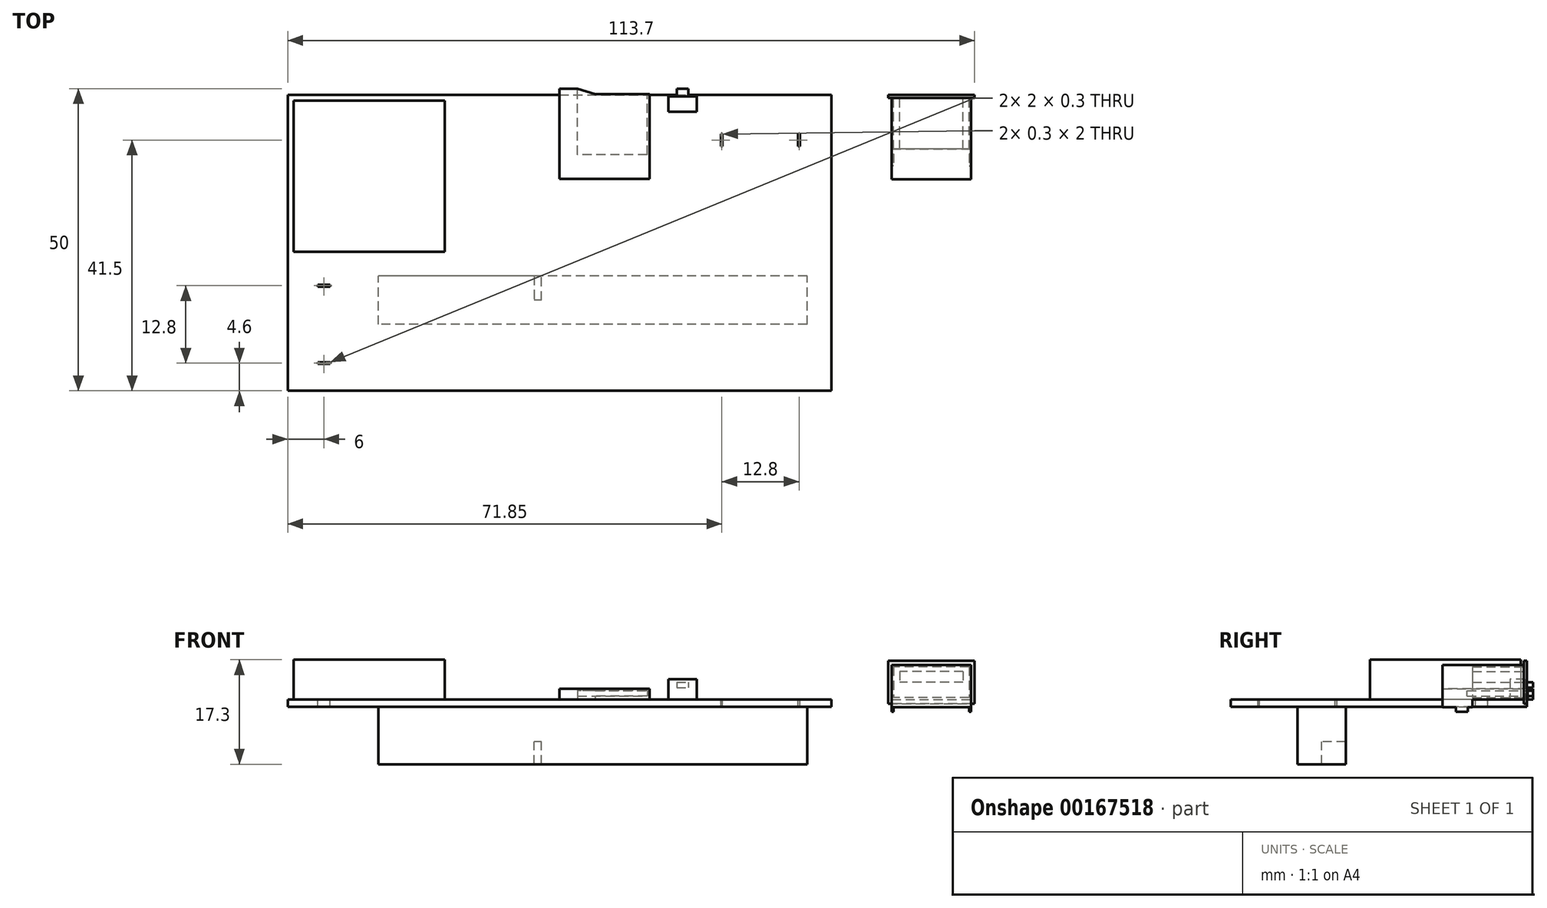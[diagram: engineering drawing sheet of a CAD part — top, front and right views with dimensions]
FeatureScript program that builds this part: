
annotation { "Feature Type Name" : "Feature", "Feature Type Description" : "" }
export const myFeature = defineFeature(function(context is Context, id is Id, definition is map)
    precondition{}
    {
        {
            var Q0;
            Q0=qCreatedBy(makeId("Top.planeOp"),FACE);
            var sketch = newSketch(context, id + "F0", { "sketchPlane" : qUnion([Q0])});
            skLineSegment(sketch, "E0.bottom", {"start": v(0, 0) * mm, "end": v(90, 0) * mm});
            skLineSegment(sketch, "E0.left", {"start": v(0, 0) * mm, "end": v(0, -49) * mm});
            skLineSegment(sketch, "E0.right", {"start": v(90, 0) * mm, "end": v(90, -49) * mm});
            skLineSegment(sketch, "E1.bottom", {"start": v(0, -49) * mm, "end": v(90, -49) * mm});
            skLineSegment(sketch, "E2.bottom", {"start": v(1, -1) * mm, "end": v(26, -1) * mm});
            skLineSegment(sketch, "E2.top", {"start": v(1, -26) * mm, "end": v(26, -26) * mm});
            skLineSegment(sketch, "E2.left", {"start": v(1, -1) * mm, "end": v(1, -26) * mm});
            skLineSegment(sketch, "E2.right", {"start": v(26, -1) * mm, "end": v(26, -26) * mm});
            skLineSegment(sketch, "E3", {"start": v(59.9, 0.1) * mm, "end": v(50.9, 0.1) * mm});
            skLineSegment(sketch, "E4", {"start": v(59.9, 0.1) * mm, "end": v(59.9, -13.9) * mm});
            skLineSegment(sketch, "E5", {"start": v(59.9, -13.9) * mm, "end": v(45, -13.9) * mm});
            skLineSegment(sketch, "E6", {"start": v(45, -13.9) * mm, "end": v(45, 1) * mm});
            skLineSegment(sketch, "E7", {"start": v(45, 1) * mm, "end": v(48, 1) * mm});
            skLineSegment(sketch, "E8", {"start": v(48, 1) * mm, "end": v(50.9, 0.1) * mm});
            skLineSegment(sketch, "E9.bottom", {"start": v(86, -38) * mm, "end": v(15, -38) * mm});
            skLineSegment(sketch, "E9.top", {"start": v(86, -30) * mm, "end": v(15, -30) * mm});
            skLineSegment(sketch, "E9.left", {"start": v(86, -38) * mm, "end": v(86, -30) * mm});
            skLineSegment(sketch, "E9.right", {"start": v(15, -38) * mm, "end": v(15, -30) * mm});
            skLineSegment(sketch, "E10", {"start": v(40.8, -30) * mm, "end": v(40.8, -34) * mm});
            skLineSegment(sketch, "E11", {"start": v(42, -34) * mm, "end": v(40.8, -34) * mm});
            skLineSegment(sketch, "E12", {"start": v(42, -34) * mm, "end": v(42, -30) * mm});
            skLineSegment(sketch, "E13.0.MirrorCS", {"start": v(63, -2.8) * mm, "end": v(67.7, -2.8) * mm});
            skLineSegment(sketch, "E13.1.MirrorCS", {"start": v(66.3, 1) * mm, "end": v(64.4, 1) * mm});
            skLineSegment(sketch, "E13.2.MirrorCS", {"start": v(66.3, -0.3) * mm, "end": v(66.3, 1) * mm});
            skLineSegment(sketch, "E13.3.MirrorCS", {"start": v(64.4, 1) * mm, "end": v(64.4, -0.3) * mm});
            skLineSegment(sketch, "E13.4.MirrorCS", {"start": v(66.3, -0.3) * mm, "end": v(67.7, -0.3) * mm});
            skLineSegment(sketch, "E13.5.MirrorCS", {"start": v(64.4, -0.3) * mm, "end": v(66.3, -0.3) * mm});
            skLineSegment(sketch, "E13.6.MirrorCS", {"start": v(63, -0.3) * mm, "end": v(64.4, -0.3) * mm});
            skLineSegment(sketch, "E13.7.MirrorCS", {"start": v(63, -0.3) * mm, "end": v(63, -2.8) * mm});
            skLineSegment(sketch, "E13.8.MirrorCS", {"start": v(67.7, -0.3) * mm, "end": v(67.7, -2.8) * mm});
            skLineSegment(sketch, "E14", {"start": v(78.25, 0) * mm, "end": v(78.25, -14.14) * mm, "construction": true});
            skLineSegment(sketch, "E15.bottom", {"start": v(71.7, -6.5) * mm, "end": v(72, -6.5) * mm});
            skLineSegment(sketch, "E15.top", {"start": v(71.7, -8.5) * mm, "end": v(72, -8.5) * mm});
            skLineSegment(sketch, "E15.left", {"start": v(71.7, -6.5) * mm, "end": v(71.7, -8.5) * mm});
            skLineSegment(sketch, "E15.right", {"start": v(72, -6.5) * mm, "end": v(72, -8.5) * mm});
            skLineSegment(sketch, "E16.0.MirrorCS", {"start": v(84.8, -6.5) * mm, "end": v(84.5, -6.5) * mm});
            skLineSegment(sketch, "E16.1.MirrorCS", {"start": v(84.8, -6.5) * mm, "end": v(84.8, -8.5) * mm});
            skLineSegment(sketch, "E16.2.MirrorCS", {"start": v(84.5, -6.5) * mm, "end": v(84.5, -8.5) * mm});
            skLineSegment(sketch, "E16.3.MirrorCS", {"start": v(84.8, -8.5) * mm, "end": v(84.5, -8.5) * mm});
            skLineSegment(sketch, "E17", {"start": v(90, -38) * mm, "end": v(0, -38) * mm, "construction": true});
            skLineSegment(sketch, "E18.bottom", {"start": v(7, -31.45) * mm, "end": v(5, -31.45) * mm});
            skLineSegment(sketch, "E18.top", {"start": v(7, -31.75) * mm, "end": v(5, -31.75) * mm});
            skLineSegment(sketch, "E18.left", {"start": v(7, -31.45) * mm, "end": v(7, -31.75) * mm});
            skLineSegment(sketch, "E18.right", {"start": v(5, -31.45) * mm, "end": v(5, -31.75) * mm});
            skLineSegment(sketch, "E19.0.MirrorCS", {"start": v(7, -44.55) * mm, "end": v(7, -44.25) * mm});
            skLineSegment(sketch, "E19.1.MirrorCS", {"start": v(7, -44.25) * mm, "end": v(5, -44.25) * mm});
            skLineSegment(sketch, "E19.2.MirrorCS", {"start": v(7, -44.55) * mm, "end": v(5, -44.55) * mm});
            skLineSegment(sketch, "E19.3.MirrorCS", {"start": v(5, -44.55) * mm, "end": v(5, -44.25) * mm});
            skSolve(sketch);
        }
        {
            var Q0;
            Q0=makeQuery(id+"F0.imprint","IMPRINT",FACE,{"disambiguationData":[TD([[makeQuery(id+"F0.imprint","IMPRINT",EDGE,{"derivedFrom":sQuery(id+"F0.wireOp",EDGE,"E0.bottom")}),-1.0]])]});
            var Q1;
            {var subQ7=sQuery(id+"F0.wireOp",EDGE,"E1.bottom");Q1=makeQuery(id+"F0.imprint","IMPRINT",FACE,{"disambiguationData":[TD([[makeQuery(id+"F0.imprint","IMPRINT",EDGE,{"derivedFrom":subQ7}),-1.0]])]});}
            var Q2;
            Q2=makeQuery(id+"F0.imprint","IMPRINT",FACE,{"disambiguationData":[TD([[makeQuery(id+"F0.imprint","IMPRINT",EDGE,{"derivedFrom":sQuery(id+"F0.wireOp",EDGE,"E2.bottom")}),-1.0]])]});
            var Q3;
            {var subQ3=sQuery(id+"F0.wireOp",EDGE,"E5");Q3=makeQuery(id+"F0.imprint","IMPRINT",FACE,{"disambiguationData":[TD([[makeQuery(id+"F0.imprint","IMPRINT",EDGE,{"derivedFrom":subQ3}),-1.0]])]});}
            var Q4;
            Q4=makeQuery(id+"F0.imprint","IMPRINT",FACE,{"disambiguationData":[TD([[makeQuery(id+"F0.imprint","IMPRINT",EDGE,{"derivedFrom":sQuery(id+"F0.wireOp",EDGE,"E9.bottom")}),-1.0]])]});
            var Q5;
            {var subQ1=sQuery(id+"F0.wireOp",EDGE,"E10");Q5=makeQuery(id+"F0.imprint","IMPRINT",FACE,{"disambiguationData":[TD([[makeQuery(id+"F0.imprint","IMPRINT",EDGE,{"derivedFrom":subQ1}),1.0]])]});}
            var Q6;
            Q6=makeQuery(id+"F0.imprint","IMPRINT",FACE,{"disambiguationData":[TD([[makeQuery(id+"F0.imprint","IMPRINT",EDGE,{"derivedFrom":sQuery(id+"F0.wireOp",EDGE,"E13.0.MirrorCS")}),1.0]])]});
            var Q7;
            {var subQ0=sQuery(id+"F0.wireOp",EDGE,"E13.5.MirrorCS");Q7=makeQuery(id+"F0.imprint","IMPRINT",FACE,{"disambiguationData":[TD([[makeQuery(id+"F0.imprint","IMPRINT",EDGE,{"derivedFrom":subQ0}),1.0]])]});}
            extrude(context, id + "F1", {"entities" : qUnion([Q0, Q1, Q2, Q3, Q4, Q5, Q6, Q7]), "oppositeDirection" : true, "depth" : 1.2 * mm});
        }
        {
            var Q0;
            Q0=makeQuery(id+"F0.imprint","IMPRINT",FACE,{"disambiguationData":[TD([[makeQuery(id+"F0.imprint","IMPRINT",EDGE,{"derivedFrom":sQuery(id+"F0.wireOp",EDGE,"E2.bottom")}),-1.0]])]});
            extrude(context, id + "F2", {"entities" : qUnion([Q0]), "operationType" : NewBodyOperationType.ADD, "depth" : 6.6 * mm});
        }
        {
            var Q0;
            {var subQ3=sQuery(id+"F0.wireOp",EDGE,"E5");Q0=makeQuery(id+"F0.imprint","IMPRINT",FACE,{"disambiguationData":[TD([[makeQuery(id+"F0.imprint","IMPRINT",EDGE,{"derivedFrom":subQ3}),-1.0]])]});}
            var Q1;
            {var subQ6=sQuery(id+"F0.wireOp",EDGE,"E3");Q1=makeQuery(id+"F0.imprint","IMPRINT",FACE,{"disambiguationData":[TD([[makeQuery(id+"F0.imprint","IMPRINT",EDGE,{"derivedFrom":subQ6}),1.0]])]});}
            extrude(context, id + "F3", {"entities" : qUnion([Q0, Q1]), "operationType" : NewBodyOperationType.ADD, "depth" : 1.8 * mm});
        }
        {
            var Q0;
            Q0=makeQuery(id+"F3.opExtrude","SWEPT_FACE",FACE,{"disambiguationData":[OSD([sQuery(id+"F0.wireOp",EDGE,"E3")])]});
            var sketch = newSketch(context, id + "F4", { "sketchPlane" : qUnion([Q0])});
            skLineSegment(sketch, "E20", {"start": v(-59.5, 1.45) * mm, "end": v(-48, 1.45) * mm});
            skLineSegment(sketch, "E21", {"start": v(-48, 1.45) * mm, "end": v(-48, 0.6) * mm});
            skLineSegment(sketch, "E22", {"start": v(-48, 0.6) * mm, "end": v(-59.5, 0.6) * mm});
            skLineSegment(sketch, "E23", {"start": v(-59.5, 0.6) * mm, "end": v(-59.5, 1.45) * mm});
            skSolve(sketch);
        }
        {
            var Q0;
            {var subQ5=sQuery(id+"F4.wireOp",EDGE,"E21");Q0=makeQuery(id+"F4.imprint","IMPRINT",FACE,{"disambiguationData":[TD([[makeQuery(id+"F4.imprint","IMPRINT",EDGE,{"derivedFrom":subQ5}),-1.0]])]});}
            var Q1;
            {var subQ5=sQuery(id+"F4.wireOp",EDGE,"E23");Q1=makeQuery(id+"F4.imprint","IMPRINT",FACE,{"disambiguationData":[TD([[makeQuery(id+"F4.imprint","IMPRINT",EDGE,{"derivedFrom":subQ5}),-1.0]])]});}
            extrude(context, id + "F5", {"entities" : qUnion([Q0, Q1]), "operationType" : NewBodyOperationType.REMOVE, "oppositeDirection" : true, "depth" : 10 * mm, "hasSecondDirection" : true, "secondDirectionOppositeDirection" : false, "secondDirectionDepth" : 3 * mm});
        }
        {
            var Q0;
            Q0=makeQuery(id+"F0.imprint","IMPRINT",FACE,{"disambiguationData":[TD([[makeQuery(id+"F0.imprint","IMPRINT",EDGE,{"derivedFrom":sQuery(id+"F0.wireOp",EDGE,"E9.bottom")}),-1.0]])]});
            extrude(context, id + "F6", {"entities" : qUnion([Q0]), "operationType" : NewBodyOperationType.ADD, "oppositeDirection" : true, "depth" : 10.7 * mm});
        }
        {
            var Q0;
            {var subQ1=sQuery(id+"F0.wireOp",EDGE,"E10");Q0=makeQuery(id+"F0.imprint","IMPRINT",FACE,{"disambiguationData":[TD([[makeQuery(id+"F0.imprint","IMPRINT",EDGE,{"derivedFrom":subQ1}),1.0]])]});}
            extrude(context, id + "F7", {"entities" : qUnion([Q0]), "operationType" : NewBodyOperationType.ADD, "oppositeDirection" : true, "depth" : 7 * mm});
        }
        {
            var Q0;
            Q0=qCreatedBy(makeId("Top.planeOp"),FACE);
            var sketch = newSketch(context, id + "F8", { "sketchPlane" : qUnion([Q0])});
            skLineSegment(sketch, "E24", {"start": v(99.4, 0) * mm, "end": v(113.7, 0) * mm});
            skLineSegment(sketch, "E25", {"start": v(113.7, 0) * mm, "end": v(113.7, -0.5) * mm});
            skLineSegment(sketch, "E26", {"start": v(113.1, -0.5) * mm, "end": v(113.1, -14) * mm});
            skLineSegment(sketch, "E27", {"start": v(113.7, -0.5) * mm, "end": v(113.1, -0.5) * mm});
            skLineSegment(sketch, "E28", {"start": v(113.1, -14) * mm, "end": v(100, -14) * mm});
            skLineSegment(sketch, "E29", {"start": v(100, -14) * mm, "end": v(100, -0.5) * mm});
            skLineSegment(sketch, "E30", {"start": v(100, -0.5) * mm, "end": v(99.4, -0.5) * mm});
            skLineSegment(sketch, "E31", {"start": v(99.4, -0.5) * mm, "end": v(99.4, 0) * mm});
            skLineSegment(sketch, "E32", {"start": v(100, -9) * mm, "end": v(113.1, -9) * mm});
            skLineSegment(sketch, "E33", {"start": v(100, -0.5) * mm, "end": v(113.1, -0.5) * mm});
            skLineSegment(sketch, "E34", {"start": v(100, -9.78) * mm, "end": v(100.3, -9.78) * mm});
            skLineSegment(sketch, "E35", {"start": v(100.3, -9.78) * mm, "end": v(100.3, -11.78) * mm});
            skLineSegment(sketch, "E36", {"start": v(100.3, -11.78) * mm, "end": v(100, -11.78) * mm});
            skLineSegment(sketch, "E37", {"start": v(106.55, -14) * mm, "end": v(106.55, 0) * mm, "construction": true});
            skLineSegment(sketch, "E38.0.MirrorCS", {"start": v(112.8, -9.78) * mm, "end": v(112.8, -11.78) * mm});
            skLineSegment(sketch, "E39.0.MirrorCS", {"start": v(113.1, -9.78) * mm, "end": v(112.8, -9.78) * mm});
            skLineSegment(sketch, "E40.0.MirrorCS", {"start": v(112.8, -11.78) * mm, "end": v(113.1, -11.78) * mm});
            skSolve(sketch);
        }
        {
            var Q0;
            {var subQ1=sQuery(id+"F8.wireOp",EDGE,"E32");Q0=makeQuery(id+"F8.imprint","IMPRINT",FACE,{"disambiguationData":[TD([[makeQuery(id+"F8.imprint","IMPRINT",EDGE,{"derivedFrom":subQ1}),1.0]])]});}
            extrude(context, id + "F9", {"entities" : qUnion([Q0]), "depth" : 5.72 * mm});
        }
        {
            var Q0;
            Q0=makeQuery(id+"F8.imprint","IMPRINT",FACE,{"disambiguationData":[TD([[makeQuery(id+"F8.imprint","IMPRINT",EDGE,{"derivedFrom":sQuery(id+"F8.wireOp",EDGE,"E24")}),-1.0]])]});
            extrude(context, id + "F10", {"entities" : qUnion([Q0]), "operationType" : NewBodyOperationType.ADD, "depth" : (5.72 + (0.5 * (7.12 - 5.72))) * mm, "hasSecondDirection" : true, "secondDirectionOppositeDirection" : true, "secondDirectionDepth" : (7.12 - 5.72) / 2 * mm});
        }
        {
            var Q0;
            {var subQ2=sQuery(id+"F8.wireOp",EDGE,"E28");Q0=makeQuery(id+"F8.imprint","IMPRINT",FACE,{"disambiguationData":[TD([[makeQuery(id+"F8.imprint","IMPRINT",EDGE,{"derivedFrom":subQ2}),-1.0]])]});}
            var Q1;
            {var subQ1=sQuery(id+"F8.wireOp",EDGE,"E34");Q1=makeQuery(id+"F8.imprint","IMPRINT",FACE,{"disambiguationData":[TD([[makeQuery(id+"F8.imprint","IMPRINT",EDGE,{"derivedFrom":subQ1}),-1.0]])]});}
            var Q2;
            Q2=makeQuery(id+"F8.imprint","IMPRINT",FACE,{"disambiguationData":[TD([[makeQuery(id+"F8.imprint","IMPRINT",EDGE,{"derivedFrom":sQuery(id+"F8.wireOp",EDGE,"E38.0.MirrorCS")}),1.0]])]});
            extrude(context, id + "F11", {"entities" : qUnion([Q0, Q1, Q2]), "operationType" : NewBodyOperationType.ADD, "depth" : 5.72 * mm, "hasSecondDirection" : true, "secondDirectionOppositeDirection" : true, "secondDirectionDepth" : (7 - 5.72) * mm});
        }
        {
            var Q0;
            Q0=makeQuery(id+"F8.imprint","IMPRINT",FACE,{"disambiguationData":[TD([[makeQuery(id+"F8.imprint","IMPRINT",EDGE,{"derivedFrom":sQuery(id+"F8.wireOp",EDGE,"E38.0.MirrorCS")}),1.0]])]});
            var Q1;
            {var subQ1=sQuery(id+"F8.wireOp",EDGE,"E34");Q1=makeQuery(id+"F8.imprint","IMPRINT",FACE,{"disambiguationData":[TD([[makeQuery(id+"F8.imprint","IMPRINT",EDGE,{"derivedFrom":subQ1}),-1.0]])]});}
            extrude(context, id + "F12", {"entities" : qUnion([Q0, Q1]), "operationType" : NewBodyOperationType.ADD, "oppositeDirection" : true, "depth" : 2 * mm});
        }
        {
            var Q0;
            Q0=makeQuery(id+"F10.opExtrude","SWEPT_FACE",FACE,{"disambiguationData":[OSD([sQuery(id+"F8.wireOp",EDGE,"E24")])]});
            var sketch = newSketch(context, id + "F13", { "sketchPlane" : qUnion([Q0])});
            skLineSegment(sketch, "E41.bottom", {"start": v(-112.8, 5.42) * mm, "end": v(-100.3, 5.42) * mm});
            skLineSegment(sketch, "E41.top", {"start": v(-112.8, 0.3) * mm, "end": v(-100.3, 0.3) * mm});
            skLineSegment(sketch, "E41.left", {"start": v(-112.8, 5.42) * mm, "end": v(-112.8, 0.3) * mm});
            skLineSegment(sketch, "E41.right", {"start": v(-100.3, 5.42) * mm, "end": v(-100.3, 0.3) * mm});
            skLineSegment(sketch, "E42", {"start": v(-100.3, 5.42) * mm, "end": v(-99.4, 5.42) * mm, "construction": true});
            skLineSegment(sketch, "E43", {"start": v(-100.3, 5.42) * mm, "end": v(-100.3, 6.42) * mm, "construction": true});
            skLineSegment(sketch, "E44", {"start": v(-112.8, 0.3) * mm, "end": v(-112.8, -0.7) * mm, "construction": true});
            skLineSegment(sketch, "E45", {"start": v(-112.8, 0.3) * mm, "end": v(-113.7, 0.3) * mm, "construction": true});
            skLineSegment(sketch, "E46.bottom", {"start": v(-111.8, 4.66) * mm, "end": v(-101.3, 4.66) * mm});
            skLineSegment(sketch, "E46.top", {"start": v(-111.8, 2.86) * mm, "end": v(-101.3, 2.86) * mm});
            skLineSegment(sketch, "E46.left", {"start": v(-111.8, 4.66) * mm, "end": v(-111.8, 2.86) * mm});
            skLineSegment(sketch, "E46.right", {"start": v(-101.3, 4.66) * mm, "end": v(-101.3, 2.86) * mm});
            skLineSegment(sketch, "E47", {"start": v(-101.3, 4.66) * mm, "end": v(-100.3, 4.66) * mm, "construction": true});
            skLineSegment(sketch, "E48", {"start": v(-111.8, 4.66) * mm, "end": v(-112.8, 4.66) * mm, "construction": true});
            skSolve(sketch);
        }
        {
            var Q0;
            Q0=makeQuery(id+"F13.imprint","IMPRINT",FACE,{"disambiguationData":[TD([[makeQuery(id+"F13.imprint","IMPRINT",EDGE,{"derivedFrom":sQuery(id+"F13.wireOp",EDGE,"E41.bottom")}),-1.0]])]});
            extrude(context, id + "F14", {"entities" : qUnion([Q0]), "operationType" : NewBodyOperationType.REMOVE, "oppositeDirection" : true, "depth" : 9 * mm});
        }
        {
            var Q0;
            Q0=makeQuery(id+"F0.imprint","IMPRINT",FACE,{"disambiguationData":[TD([[makeQuery(id+"F0.imprint","IMPRINT",EDGE,{"derivedFrom":sQuery(id+"F0.wireOp",EDGE,"E13.0.MirrorCS")}),1.0]])]});
            extrude(context, id + "F15", {"entities" : qUnion([Q0]), "operationType" : NewBodyOperationType.ADD, "depth" : 3.35 * mm});
        }
        {
            var Q0;
            {var subQ3=sQuery(id+"F0.wireOp",EDGE,"E13.1.MirrorCS");Q0=makeQuery(id+"F0.imprint","IMPRINT",FACE,{"disambiguationData":[TD([[makeQuery(id+"F0.imprint","IMPRINT",EDGE,{"derivedFrom":subQ3}),1.0]])]});}
            var Q1;
            {var subQ0=sQuery(id+"F0.wireOp",EDGE,"E13.5.MirrorCS");Q1=makeQuery(id+"F0.imprint","IMPRINT",FACE,{"disambiguationData":[TD([[makeQuery(id+"F0.imprint","IMPRINT",EDGE,{"derivedFrom":subQ0}),1.0]])]});}
            extrude(context, id + "F16", {"entities" : qUnion([Q0, Q1]), "operationType" : NewBodyOperationType.ADD, "depth" : 2.85 * mm, "hasSecondDirection" : true, "secondDirectionOppositeDirection" : false, "secondDirectionDepth" : 1.95 * mm});
        }
    });
